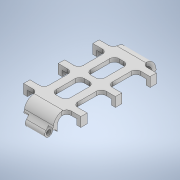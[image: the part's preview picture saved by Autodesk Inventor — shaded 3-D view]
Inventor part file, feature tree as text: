
AUTODESK INVENTOR PART (.ipt)
format: ipt  version: 2022 (Build 260153000, 153)  size: 580,096 bytes
history: native  units: mm
features: extrude x17, sketch x17, mirror x8, fillet x4, pattern_linear x1
ambient origin geometry x8: Origin, YZ Plane, XZ Plane, XY Plane, X Axis, Y Axis, Z Axis, Center Point
bodies: Solid1 (feature_tree)
feature tree (47):
  extrude  "Extrusion1"  Depth=15.4mm
  extrude  "Extrusion2"  Depth=1.5mm
  extrude  "Extrusion3"  Depth=6.0mm
  mirror  "Mirror1"
  mirror  "Mirror2"
  extrude  "Extrusion4"  Depth=1.0mm
  extrude  "Extrusion5"  Depth=3.0mm
  extrude  "Extrusion6"  Depth=16.0mm
  extrude  "Extrusion7"  Depth=3.0mm
  extrude  "Extrusion8"  Depth=1.0mm
  extrude  "Extrusion9"  Depth=1.0mm TaperAngle=0.0deg
  mirror  "Mirror4"
  extrude  "Extrusion11"  Depth=4.0mm TaperAngle=0.0deg
  extrude  "Extrusion12"  Depth=3.0mm
  mirror  "Mirror5"
  mirror  "Mirror6"
  pattern_linear  "Rectangular Pattern1"  Spacing1=3.0mm  [1 undecoded]
  extrude  "Extrusion13"  Depth=1.0mm TaperAngle=0.0deg
  extrude  "Extrusion14"  Depth=1.0mm
  extrude  "Extrusion15"  Depth=1.0mm
  mirror  "Mirror7"
  extrude  "Extrusion16"  Depth=1.0mm
  extrude  "Extrusion17"  Depth=1.0mm
  extrude  "Extrusion18"  TaperAngle=0.0deg  [1 undecoded]
  mirror  "Mirror8"
  fillet  "Fillet1"  Radius=2.5mm
  fillet  "Fillet2"  Radius=12.5mm
  mirror  "Mirror9"
  fillet  "Fillet3"  Radius=15.0mm
  fillet  "Fillet4"  Radius=7.5mm
  sketch  "Sketch1"  dims[d0=36.5mm d1=15.4mm d2=7.7mm]
  sketch  "Sketch2"  dims[d5=1.5mm d9=1.5mm]
  sketch  "Sketch4"  dims[d12=2.0mm d13=6.0mm]
  sketch  "Sketch5"  dims[d14=1.0mm d15=1.0mm]
  sketch  "Sketch6"  dims[d16=2.5mm d17=3.0mm]
  sketch  "Sketch7"  dims[d20=9.5mm d21=16.0mm]
  sketch  "Sketch8"  dims[d22=0.0mm d23=3.0mm]
  sketch  "Sketch9"  dims[d24=3.0mm d25=1.0mm]
  sketch  "Sketch10"  dims[d26=1.0mm d27=2.0mm d28=0.0mm]
  sketch  "Sketch11"  dims[d29=2.0mm d30=4.0mm d31=0.0mm]
  sketch  "Sketch12"  dims[d32=6.5mm d33=3.0mm]
  sketch  "Sketch13"  dims[d34=2.0mm]
  sketch  "Sketch14"  dims[d35=2.0mm]
  sketch  "Sketch15"  dims[d36=2.0mm d37=0.0mm]
  sketch  "Sketch17"  dims[d38=6.0mm]
  sketch  "Sketch18"  dims[d41=3.0mm]
  sketch  "Sketch19"  dims[d42=3.0mm d43=3.0mm d44=2.0mm d45=0.0mm d46=60.0mm d47=30.5mm d48=15.25mm d49=30.0mm d50=0.0mm d51=0.0mm d52=2.5mm d53=12.5mm d54=0.0mm d55=15.0mm d56=7.5mm d57=3.75mm d58=12.5mm d59=0.0mm d60=0.0mm d61=0.0mm d62=9.0mm d63=20.0mm d64=4.7mm d65=10.0mm d66=0.0mm d67=2.0mm d68=3.0mm d69=3.0mm d70=3.0mm d75=6.5mm d76=2.0mm d77=2.5mm d78=0.0mm d79=6.0mm d80=3.0mm d83=6.0mm d84=2.5mm d85=0.0mm d86=30.0mm d88=22.0mm d89=0.0mm d90=0.0mm d91=0.0mm d92=0.0mm d93=10.0mm d94=0.0mm d95=5.0mm d96=3.0mm d97=7.0mm d98=2.5mm d99=0.0mm d100=0.0mm d101=10.0mm d102=0.0mm d103=5.2mm d104=3.0mm d105=0.0mm d106=5.5mm d107=1.0mm d108=5.5mm d109=1.0mm]
note: 2 required parameter values undecoded (feature->parameter linkage not recoverable at this tier; creation-order binding heuristic only, values carry confidence <= 0.55)
